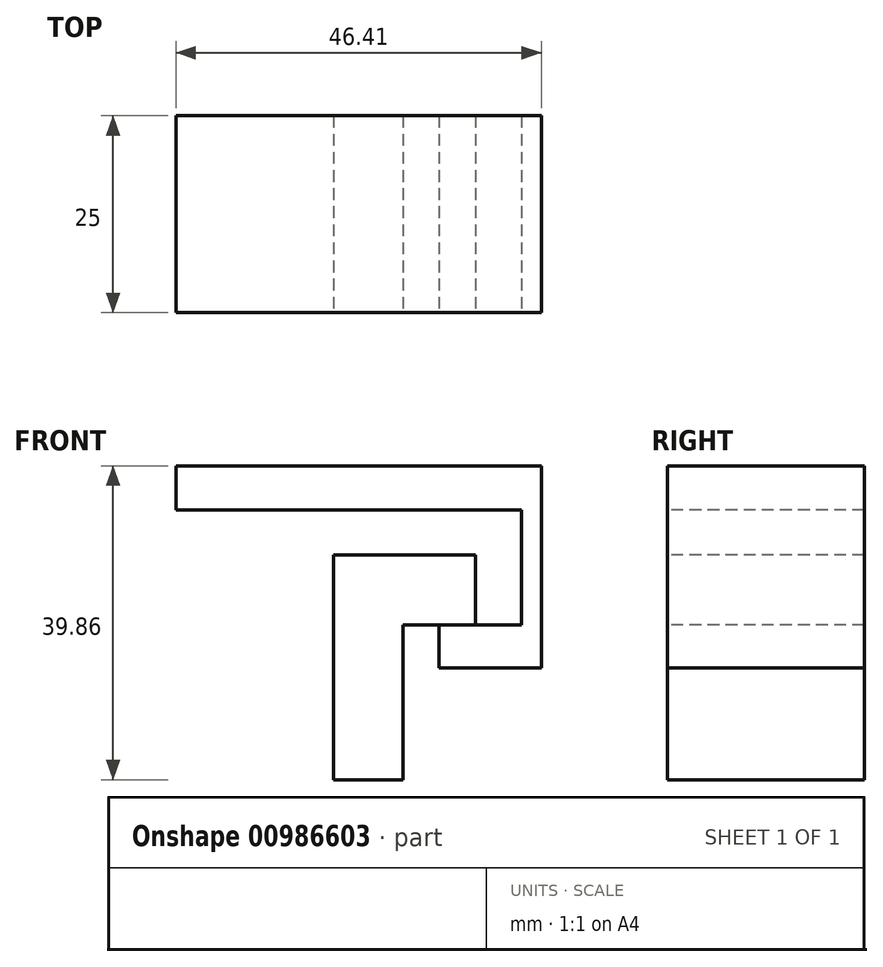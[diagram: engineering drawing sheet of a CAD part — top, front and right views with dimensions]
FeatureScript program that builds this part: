
annotation { "Feature Type Name" : "Feature", "Feature Type Description" : "" }
export const myFeature = defineFeature(function(context is Context, id is Id, definition is map)
    precondition{}
    {
        {
            var Q0;
            Q0=qCreatedBy(makeId("Front.planeOp"),FACE);
            var sketch = newSketch(context, id + "F0", { "sketchPlane" : qUnion([Q0])});
            skLineSegment(sketch, "E0", {"start": v(0, 28.55) * mm, "end": v(0, 0) * mm});
            skLineSegment(sketch, "E1", {"start": v(0, 28.55) * mm, "end": v(18.03, 28.55) * mm});
            skLineSegment(sketch, "E2", {"start": v(18.03, 28.55) * mm, "end": v(18.03, 19.64) * mm});
            skLineSegment(sketch, "E3", {"start": v(18.03, 19.64) * mm, "end": v(8.83, 19.64) * mm});
            skLineSegment(sketch, "E4", {"start": v(8.83, 19.64) * mm, "end": v(8.83, 0) * mm});
            skLineSegment(sketch, "E5", {"start": v(8.83, 0) * mm, "end": v(0, 0) * mm});
            skSolve(sketch);
        }
        {
            var Q0;
            Q0=qSketchRegion(id+"F0",true);
            extrude(context, id + "F1", {"entities" : qUnion([Q0]), "oppositeDirection" : true, "depth" : 25 * mm, "offsetDistance" : 25 * mm});
        }
        {
            var Q0;
            Q0=makeQuery(id+"F1.opExtrude","CAP_FACE",FACE,{"disambiguationData":[OSD([sQuery(id+"F0.wireOp",EDGE,"E0"),sQuery(id+"F0.wireOp",EDGE,"E1"),sQuery(id+"F0.wireOp",EDGE,"E2"),sQuery(id+"F0.wireOp",EDGE,"E3"),sQuery(id+"F0.wireOp",EDGE,"E4"),sQuery(id+"F0.wireOp",EDGE,"E5")])],"isStart":true});
            var sketch = newSketch(context, id + "F2", { "sketchPlane" : qUnion([Q0])});
            skLineSegment(sketch, "E6", {"start": v(13.43, 19.64) * mm, "end": v(26.42, 19.64) * mm});
            skLineSegment(sketch, "E7", {"start": v(26.42, 19.64) * mm, "end": v(26.42, 39.86) * mm});
            skLineSegment(sketch, "E8", {"start": v(26.42, 39.86) * mm, "end": v(-20, 39.86) * mm});
            skLineSegment(sketch, "E9", {"start": v(-20, 39.86) * mm, "end": v(-20, 34.29) * mm});
            skLineSegment(sketch, "E10", {"start": v(-20, 34.29) * mm, "end": v(23.86, 34.29) * mm});
            skLineSegment(sketch, "E11", {"start": v(23.86, 34.29) * mm, "end": v(23.86, 19.64) * mm});
            skLineSegment(sketch, "E12", {"start": v(13.43, 19.64) * mm, "end": v(13.43, 14.2) * mm});
            skLineSegment(sketch, "E13", {"start": v(13.43, 14.2) * mm, "end": v(26.42, 14.2) * mm});
            skLineSegment(sketch, "E14", {"start": v(26.42, 14.2) * mm, "end": v(26.42, 19.64) * mm});
            skSolve(sketch);
        }
        {
            var Q0;
            Q0=qSketchRegion(id+"F2",true);
            extrude(context, id + "F3", {"entities" : qUnion([Q0]), "oppositeDirection" : true, "depth" : 25 * mm, "offsetDistance" : 25 * mm});
        }
    });
